# Revit family: PRD_FrankeWS_Mrrs_Mirror_M501HD
name_source: partatom
category: Furniture
revit_build: Autodesk Revit 2018 (Build: 20190510_1515(x64)
units: mm (PartAtom-declared; Revit-internal decimal feet)

## family parameters
Cut with Voids When Loaded = No
Host = Face
OmniClass Number = 23.40.20.21
OmniClass Title = Toilet and Bath Specialties
Room Calculation Point = No
Shared = No

## types (1)
- M501HD
    AssetType = Fixed
    BIMObjectName = PRD_AR_Mirrors_Mirror_M501HD
    Category = Pr_25_71_53_06, Bathroom mirrors
    Color = Stainless steel
    Default Elevation = 1100 mm
    Description = Stainless steel mirror for wall mounting, mirror with a reflective polished surface, material thickness 1 mm, mirror surface tilted towards user, six visible fixation points, incl. stainless steel screws and dowels.
    DurationUnit = year
    Features = stainless steel, 1.00 mm, high polished, wall mounting, 460x528x62 mm (WxHxD)
    Finish = High polished
    Form = Wall mounted
    GrossWeight = 3.00 kg
    IfcExportAs = IfcFurnitureType
    IfcExportType = NOTDEFINED
    IntegralAccessories = Stainless steel screws and dowels incl.
    MainColor = Stainless steel
    Manufacturer = KWC Group AG
    ManufacturerName = KWC Group AG
    ManufacturerURL = www.kwc.com
    Material = Stainless steel
    MaterialsFrame = Stainless steel 1.4301
    MaterialsGlazing = Stainless steel 1.4301
    MirrorMaterial = PRD_AR_StainlessSteel_HighPolished
    Model = M501HD
    ModelNumber = 2000103195
    ModelReference = M501HD
    NBSDescription = Mirrors
    NBSReference = 45-35-72/336
    Name = Mirror M501HD
    NetWeight = 2.60 kg
    NominalDepth = 62 mm  [stored 0.203412 ft]
    NominalHeight = 528 mm  [stored 1.73228 ft]
    NominalLength = 460 mm  [stored 1.50919 ft]
    NominalWidth = 460 mm  [stored 1.50919 ft]
    ProductInformation = https://pim.kwc.com
    Size = 460 x 528 x 62 mm
    Style = Mirror
    TypeOfFixing = Screw
    URL = www.kwc.com
    Uniclass2015Code = Pr_25_71_53_06
    Uniclass2015Title = Bathroom mirrors
    Uniclass2015Version = Products v1.5
    Version = 1
    WarrantyDurationUnit = year

note: [stored X ft] marks values corroborated as IEEE doubles in the binary element streams (Revit-internal decimal feet)

## geometry (parser evidence)
native form markers: Sweep x2
no freeform markers — native parametric forms only
